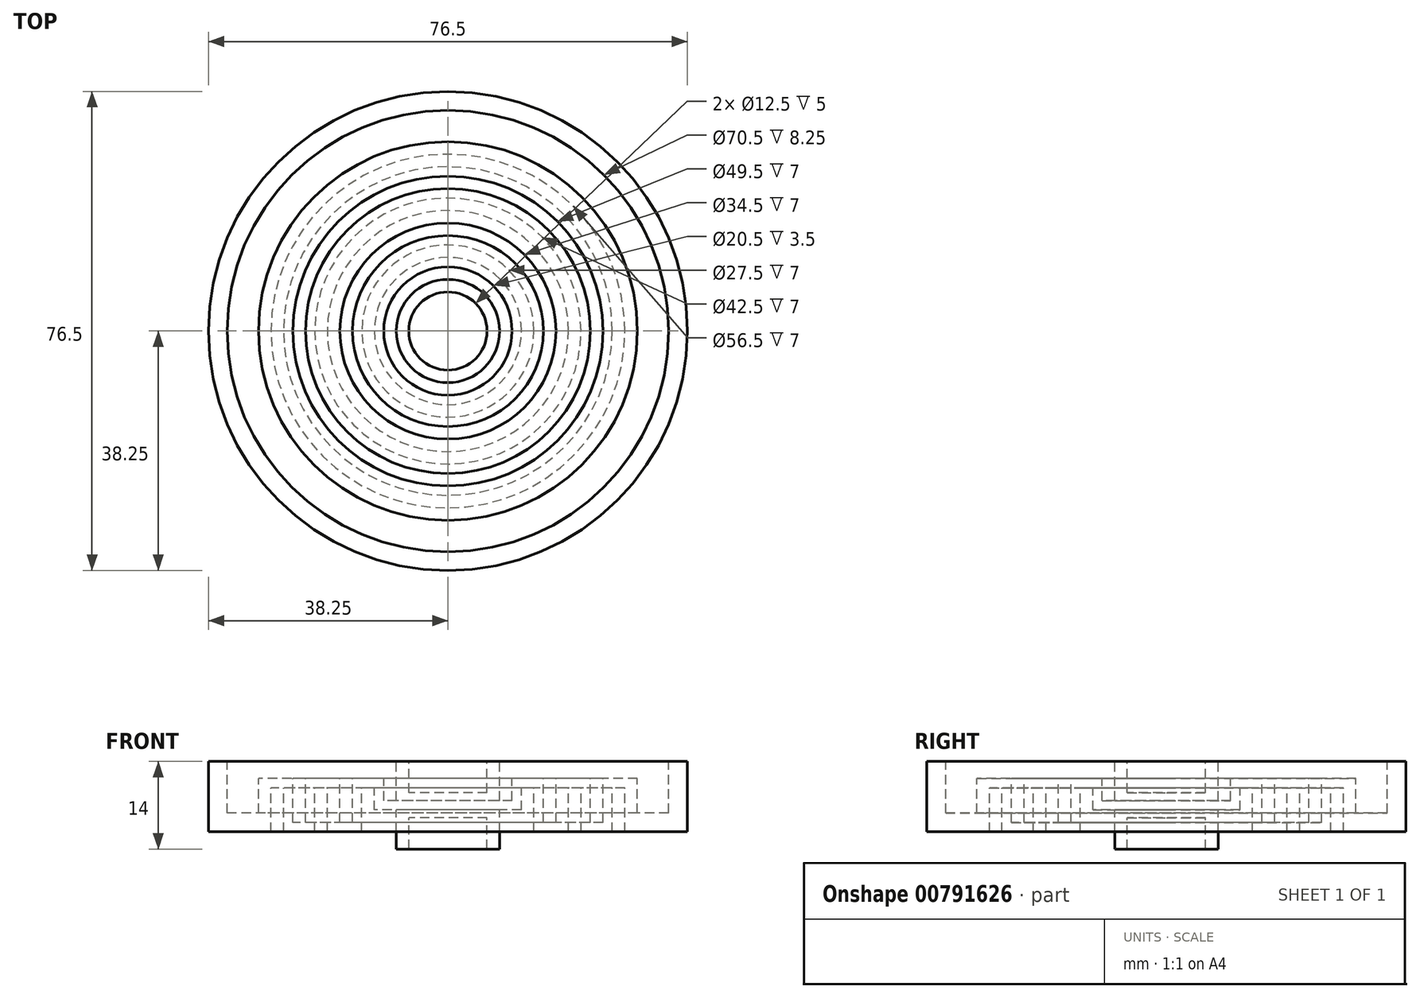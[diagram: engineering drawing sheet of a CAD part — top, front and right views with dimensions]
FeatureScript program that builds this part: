
annotation { "Feature Type Name" : "Feature", "Feature Type Description" : "" }
export const myFeature = defineFeature(function(context is Context, id is Id, definition is map)
    precondition{}
    {
        {
            var Q0;
            Q0=qCreatedBy(makeId("Front.planeOp"),FACE);
            var sketch = newSketch(context, id + "F0", { "sketchPlane" : qUnion([Q0])});
            skLineSegment(sketch, "E0.bottom", {"start": v(0, 0) * mm, "end": v(6.25, 0) * mm});
            skLineSegment(sketch, "E0.top", {"start": v(0, -2) * mm, "end": v(6.25, -2) * mm});
            skLineSegment(sketch, "E0.left", {"start": v(0, 0) * mm, "end": v(0, -2) * mm});
            skLineSegment(sketch, "E0.right", {"start": v(6.25, 0) * mm, "end": v(6.25, -2) * mm});
            skLineSegment(sketch, "E1.top", {"start": v(0, 2) * mm, "end": v(6.25, 2) * mm});
            skLineSegment(sketch, "E1.left", {"start": v(0, 0) * mm, "end": v(0, 2) * mm});
            skLineSegment(sketch, "E1.right", {"start": v(6.25, 0) * mm, "end": v(6.25, 2) * mm});
            skLineSegment(sketch, "E2.bottom", {"start": v(6.25, 0) * mm, "end": v(8.25, 0) * mm});
            skLineSegment(sketch, "E2.top", {"start": v(6.25, 7) * mm, "end": v(8.25, 7) * mm});
            skLineSegment(sketch, "E2.left", {"start": v(6.25, 0) * mm, "end": v(6.25, 7) * mm});
            skLineSegment(sketch, "E2.right", {"start": v(8.25, 0) * mm, "end": v(8.25, 7) * mm});
            skLineSegment(sketch, "E3.top", {"start": v(6.25, -7) * mm, "end": v(8.25, -7) * mm});
            skLineSegment(sketch, "E3.left", {"start": v(6.25, 0) * mm, "end": v(6.25, -7) * mm});
            skLineSegment(sketch, "E3.right", {"start": v(8.25, 0) * mm, "end": v(8.25, -7) * mm});
            skLineSegment(sketch, "E4.bottom", {"start": v(8.25, 0) * mm, "end": v(10.25, 0) * mm});
            skLineSegment(sketch, "E4.top", {"start": v(8.25, 0.75) * mm, "end": v(10.25, 0.75) * mm});
            skLineSegment(sketch, "E4.left", {"start": v(8.25, 0) * mm, "end": v(8.25, 0.75) * mm});
            skLineSegment(sketch, "E4.right", {"start": v(10.25, 0) * mm, "end": v(10.25, 0.75) * mm});
            skLineSegment(sketch, "E5.bottom", {"start": v(10.25, 0) * mm, "end": v(8.25, 0) * mm});
            skLineSegment(sketch, "E5.top", {"start": v(10.25, -0.75) * mm, "end": v(8.25, -0.75) * mm});
            skLineSegment(sketch, "E5.left", {"start": v(10.25, 0) * mm, "end": v(10.25, -0.75) * mm});
            skLineSegment(sketch, "E5.right", {"start": v(8.25, 0) * mm, "end": v(8.25, -0.75) * mm});
            skLineSegment(sketch, "E6.bottom", {"start": v(10.25, -0.75) * mm, "end": v(11.75, -0.75) * mm});
            skLineSegment(sketch, "E7", {"start": v(0, 20.38) * mm, "end": v(25.15, 20.38) * mm});
            skLineSegment(sketch, "E8", {"start": v(25.15, 20.38) * mm, "end": v(25.15, 18.23) * mm});
            skLineSegment(sketch, "E9.top", {"start": v(10.25, 4.25) * mm, "end": v(11.75, 4.25) * mm});
            skLineSegment(sketch, "E9.left", {"start": v(10.25, -0.75) * mm, "end": v(10.25, 4.25) * mm});
            skLineSegment(sketch, "E9.right", {"start": v(11.75, -0.75) * mm, "end": v(11.75, 4.25) * mm});
            skLineSegment(sketch, "E10.bottom", {"start": v(11.75, 4.25) * mm, "end": v(13.75, 4.25) * mm});
            skLineSegment(sketch, "E10.top", {"start": v(11.75, 2.75) * mm, "end": v(13.75, 2.75) * mm});
            skLineSegment(sketch, "E10.left", {"start": v(11.75, 4.25) * mm, "end": v(11.75, 2.75) * mm});
            skLineSegment(sketch, "E10.right", {"start": v(13.75, 4.25) * mm, "end": v(13.75, 2.75) * mm});
            skLineSegment(sketch, "E11.bottom", {"start": v(13.75, 4.25) * mm, "end": v(15.25, 4.25) * mm});
            skLineSegment(sketch, "E11.top", {"start": v(13.75, -4.25) * mm, "end": v(15.25, -4.25) * mm});
            skLineSegment(sketch, "E11.left", {"start": v(13.75, 4.25) * mm, "end": v(13.75, -4.25) * mm});
            skLineSegment(sketch, "E11.right", {"start": v(15.25, 4.25) * mm, "end": v(15.25, -4.25) * mm});
            skLineSegment(sketch, "E12.bottom", {"start": v(15.25, -4.25) * mm, "end": v(17.25, -4.25) * mm});
            skLineSegment(sketch, "E12.top", {"start": v(15.25, -2.75) * mm, "end": v(17.25, -2.75) * mm});
            skLineSegment(sketch, "E12.left", {"start": v(15.25, -4.25) * mm, "end": v(15.25, -2.75) * mm});
            skLineSegment(sketch, "E12.right", {"start": v(17.25, -4.25) * mm, "end": v(17.25, -2.75) * mm});
            skLineSegment(sketch, "E13.bottom", {"start": v(17.25, -4.25) * mm, "end": v(19.25, -4.25) * mm});
            skLineSegment(sketch, "E13.top", {"start": v(17.25, 4.25) * mm, "end": v(19.25, 4.25) * mm});
            skLineSegment(sketch, "E13.left", {"start": v(17.25, -4.25) * mm, "end": v(17.25, 4.25) * mm});
            skLineSegment(sketch, "E13.right", {"start": v(19.25, -4.25) * mm, "end": v(19.25, 4.25) * mm});
            skLineSegment(sketch, "E14.bottom", {"start": v(19.25, 4.25) * mm, "end": v(21.25, 4.25) * mm});
            skLineSegment(sketch, "E14.top", {"start": v(19.25, 2.75) * mm, "end": v(21.25, 2.75) * mm});
            skLineSegment(sketch, "E14.left", {"start": v(19.25, 4.25) * mm, "end": v(19.25, 2.75) * mm});
            skLineSegment(sketch, "E14.right", {"start": v(21.25, 4.25) * mm, "end": v(21.25, 2.75) * mm});
            skLineSegment(sketch, "E15.bottom", {"start": v(21.25, 4.25) * mm, "end": v(22.75, 4.25) * mm});
            skLineSegment(sketch, "E15.top", {"start": v(21.25, -4.25) * mm, "end": v(22.75, -4.25) * mm});
            skLineSegment(sketch, "E15.left", {"start": v(21.25, 4.25) * mm, "end": v(21.25, -4.25) * mm});
            skLineSegment(sketch, "E15.right", {"start": v(22.75, 4.25) * mm, "end": v(22.75, -4.25) * mm});
            skLineSegment(sketch, "E16.bottom", {"start": v(22.75, -4.25) * mm, "end": v(24.75, -4.25) * mm});
            skLineSegment(sketch, "E16.top", {"start": v(22.75, -2.75) * mm, "end": v(24.75, -2.75) * mm});
            skLineSegment(sketch, "E16.left", {"start": v(22.75, -4.25) * mm, "end": v(22.75, -2.75) * mm});
            skLineSegment(sketch, "E16.right", {"start": v(24.75, -4.25) * mm, "end": v(24.75, -2.75) * mm});
            skLineSegment(sketch, "E17.bottom", {"start": v(24.75, -4.25) * mm, "end": v(26.25, -4.25) * mm});
            skLineSegment(sketch, "E17.top", {"start": v(24.75, 4.25) * mm, "end": v(26.25, 4.25) * mm});
            skLineSegment(sketch, "E17.left", {"start": v(24.75, -4.25) * mm, "end": v(24.75, 4.25) * mm});
            skLineSegment(sketch, "E17.right", {"start": v(26.25, -4.25) * mm, "end": v(26.25, 4.25) * mm});
            skLineSegment(sketch, "E18.bottom", {"start": v(26.25, 4.25) * mm, "end": v(28.25, 4.25) * mm});
            skLineSegment(sketch, "E18.top", {"start": v(26.25, 2.75) * mm, "end": v(28.25, 2.75) * mm});
            skLineSegment(sketch, "E18.left", {"start": v(26.25, 4.25) * mm, "end": v(26.25, 2.75) * mm});
            skLineSegment(sketch, "E18.right", {"start": v(28.25, 4.25) * mm, "end": v(28.25, 2.75) * mm});
            skLineSegment(sketch, "E19.bottom", {"start": v(28.25, 4.25) * mm, "end": v(30.25, 4.25) * mm});
            skLineSegment(sketch, "E19.top", {"start": v(28.25, -4.25) * mm, "end": v(30.25, -4.25) * mm});
            skLineSegment(sketch, "E19.left", {"start": v(28.25, 4.25) * mm, "end": v(28.25, -4.25) * mm});
            skLineSegment(sketch, "E19.right", {"start": v(30.25, 4.25) * mm, "end": v(30.25, -4.25) * mm});
            skLineSegment(sketch, "E20.bottom", {"start": v(30.25, -4.25) * mm, "end": v(35.25, -4.25) * mm});
            skLineSegment(sketch, "E20.top", {"start": v(30.25, -1.25) * mm, "end": v(35.25, -1.25) * mm});
            skLineSegment(sketch, "E20.left", {"start": v(30.25, -4.25) * mm, "end": v(30.25, -1.25) * mm});
            skLineSegment(sketch, "E20.right", {"start": v(35.25, -4.25) * mm, "end": v(35.25, -1.25) * mm});
            skLineSegment(sketch, "E21.bottom", {"start": v(35.25, -4.25) * mm, "end": v(38.25, -4.25) * mm});
            skLineSegment(sketch, "E21.top", {"start": v(35.25, 7) * mm, "end": v(38.25, 7) * mm});
            skLineSegment(sketch, "E21.left", {"start": v(35.25, -4.25) * mm, "end": v(35.25, 7) * mm});
            skLineSegment(sketch, "E21.right", {"start": v(38.25, -4.25) * mm, "end": v(38.25, 7) * mm});
            skSolve(sketch);
        }
        {
            var Q0;
            Q0=qCreatedBy(makeId("Front.planeOp"),FACE);
            var sketch = newSketch(context, id + "F1", { "sketchPlane" : qUnion([Q0])});
            skLineSegment(sketch, "E22", {"start": v(0, 8.48) * mm, "end": v(0, -12.49) * mm});
            skSolve(sketch);
        }
        {
            var Q0;
            Q0 = qSketchRegion(id + "F0", true);
            var Q1;
            Q1=sQuery(id+"F1.wireOp",EDGE,"E22");
            revolve(context, id + "F2", {"surfaceOperationType" : NewSurfaceOperationType.NEW, "entities" : qUnion([Q0]), "axis" : qUnion([Q1]), "revolveType" : RevolveType.FULL});
        }
    });
